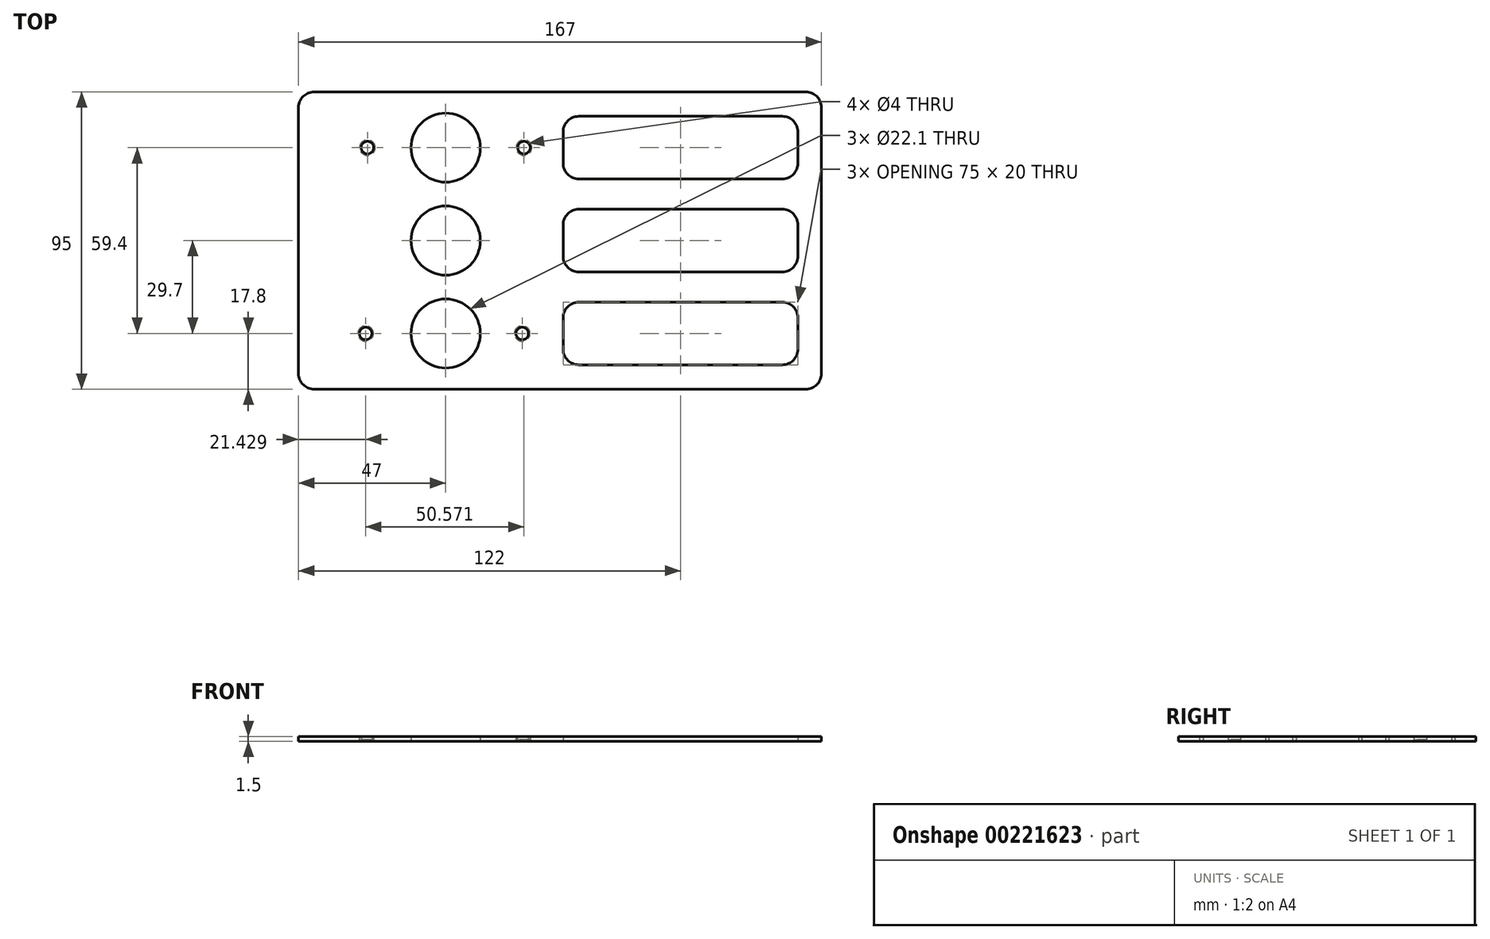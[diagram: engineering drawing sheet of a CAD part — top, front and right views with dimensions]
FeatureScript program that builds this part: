
annotation { "Feature Type Name" : "Feature", "Feature Type Description" : "" }
export const myFeature = defineFeature(function(context is Context, id is Id, definition is map)
    precondition{}
    {
        {
            var Q0;
            Q0=qCreatedBy(makeId("Top.planeOp"),FACE);
            var sketch = newSketch(context, id + "F0", { "sketchPlane" : qUnion([Q0])});
            skPoint(sketch, "E0.middle", {"position": v(0, 0) * mm});
            skCircle(sketch, "E1", {"center": v(-25, 29.7) * mm, "radius": 2 * mm});
            skCircle(sketch, "E2", {"center": v(25, 29.7) * mm, "radius": 2 * mm});
            skCircle(sketch, "E3", {"center": v(-25.57, -29.7) * mm, "radius": 2 * mm});
            skCircle(sketch, "E4", {"center": v(24.43, -29.7) * mm, "radius": 2 * mm});
            skLineSegment(sketch, "E5.bottom", {"start": v(-47, 47.5) * mm, "end": v(120, 47.5) * mm});
            skLineSegment(sketch, "E5.top", {"start": v(-47, -47.5) * mm, "end": v(120, -47.5) * mm});
            skLineSegment(sketch, "E5.left", {"start": v(-47, 47.5) * mm, "end": v(-47, -47.5) * mm});
            skLineSegment(sketch, "E5.right", {"start": v(120, 47.5) * mm, "end": v(120, -47.5) * mm});
            skPoint(sketch, "E5.middle", {"position": v(36.5, 0) * mm});
            skCircle(sketch, "E6", {"center": v(0, 29.7) * mm, "radius": 11.05 * mm});
            skCircle(sketch, "E7", {"center": v(0, 0) * mm, "radius": 11.05 * mm});
            skCircle(sketch, "E8", {"center": v(0, -29.7) * mm, "radius": 11.05 * mm});
            skLineSegment(sketch, "E9.bottom", {"start": v(112.5, 39.7) * mm, "end": v(37.5, 39.7) * mm});
            skLineSegment(sketch, "E9.top", {"start": v(112.5, 19.7) * mm, "end": v(37.5, 19.7) * mm});
            skLineSegment(sketch, "E9.left", {"start": v(112.5, 39.7) * mm, "end": v(112.5, 19.7) * mm});
            skLineSegment(sketch, "E9.right", {"start": v(37.5, 39.7) * mm, "end": v(37.5, 19.7) * mm});
            skPoint(sketch, "E9.middle", {"position": v(75, 29.7) * mm});
            skLineSegment(sketch, "E10.bottom", {"start": v(112.5, 10) * mm, "end": v(37.5, 10) * mm});
            skLineSegment(sketch, "E10.top", {"start": v(112.5, -10) * mm, "end": v(37.5, -10) * mm});
            skLineSegment(sketch, "E10.left", {"start": v(112.5, 10) * mm, "end": v(112.5, -10) * mm});
            skLineSegment(sketch, "E10.right", {"start": v(37.5, 10) * mm, "end": v(37.5, -10) * mm});
            skPoint(sketch, "E10.middle", {"position": v(75, 0) * mm});
            skPoint(sketch, "E10.middle.positionSnap0", {"position": v(75, 19.7) * mm});
            skPoint(sketch, "E10.centerSnap0", {"position": v(75, 19.7) * mm});
            skLineSegment(sketch, "E11.bottom", {"start": v(112.5, -19.7) * mm, "end": v(37.5, -19.7) * mm});
            skLineSegment(sketch, "E11.top", {"start": v(112.5, -39.7) * mm, "end": v(37.5, -39.7) * mm});
            skLineSegment(sketch, "E11.left", {"start": v(112.5, -19.7) * mm, "end": v(112.5, -39.7) * mm});
            skLineSegment(sketch, "E11.right", {"start": v(37.5, -19.7) * mm, "end": v(37.5, -39.7) * mm});
            skPoint(sketch, "E11.middle", {"position": v(75, -29.7) * mm});
            skSolve(sketch);
        }
        {
            var Q0;
            Q0=makeQuery(id+"F0.imprint","IMPRINT",FACE,{"disambiguationData":[TD([[makeQuery(id+"F0.imprint","IMPRINT",EDGE,{"derivedFrom":sQuery(id+"F0.wireOp",EDGE,"NzcNvOOA-lG1h-x87r-AjBX-t4IytyfyV268")}),-1.0]])]});
            var Q1;
            Q1=makeQuery(id+"F0.imprint","IMPRINT",FACE,{"disambiguationData":[TD([[makeQuery(id+"F0.imprint","IMPRINT",EDGE,{"derivedFrom":sQuery(id+"F0.wireOp",EDGE,"E1")}),-1.0]])]});
            extrude(context, id + "F1", {"entities" : qUnion([Q0, Q1]), "endBound" : BoundingType.SYMMETRIC, "offsetDistance" : 25 * mm, "depth" : 1.5 * mm});
        }
        {
            var Q0;
            Q0=makeQuery(id+"F1.opExtrude","SWEPT_EDGE",EDGE,{"disambiguationData":[OSD([sQuery(id+"F0.wireOp",EDGE,"E5.bottom"),sQuery(id+"F0.wireOp",EDGE,"E5.right")])]});
            var Q1;
            Q1=makeQuery(id+"F1.opExtrude","SWEPT_EDGE",EDGE,{"disambiguationData":[OSD([sQuery(id+"F0.wireOp",EDGE,"E5.top"),sQuery(id+"F0.wireOp",EDGE,"E5.right")])]});
            var Q2;
            Q2=makeQuery(id+"F1.opExtrude","SWEPT_EDGE",EDGE,{"disambiguationData":[OSD([sQuery(id+"F0.wireOp",EDGE,"E5.top"),sQuery(id+"F0.wireOp",EDGE,"E5.left")])]});
            var Q3;
            Q3=makeQuery(id+"F1.opExtrude","SWEPT_EDGE",EDGE,{"disambiguationData":[OSD([sQuery(id+"F0.wireOp",EDGE,"E5.bottom"),sQuery(id+"F0.wireOp",EDGE,"E5.left")])]});
            fillet(context, id + "F2", {"entities" : qUnion([Q0, Q1, Q2, Q3]), "radius" : 5 * mm, "tangentPropagation" : true, "allowEdgeOverflow" : false});
        }
        {
            var Q0;
            Q0=makeQuery(id+"F1.opExtrude","SWEPT_EDGE",EDGE,{"disambiguationData":[OSD([sQuery(id+"F0.wireOp",EDGE,"E9.bottom"),sQuery(id+"F0.wireOp",EDGE,"E9.right")])]});
            var Q1;
            Q1=makeQuery(id+"F1.opExtrude","SWEPT_EDGE",EDGE,{"disambiguationData":[OSD([sQuery(id+"F0.wireOp",EDGE,"E10.bottom"),sQuery(id+"F0.wireOp",EDGE,"E10.right")])]});
            var Q2;
            Q2=makeQuery(id+"F1.opExtrude","SWEPT_EDGE",EDGE,{"disambiguationData":[OSD([sQuery(id+"F0.wireOp",EDGE,"E11.bottom"),sQuery(id+"F0.wireOp",EDGE,"E11.right")])]});
            var Q3;
            Q3=makeQuery(id+"F1.opExtrude","SWEPT_EDGE",EDGE,{"disambiguationData":[OSD([sQuery(id+"F0.wireOp",EDGE,"E9.bottom"),sQuery(id+"F0.wireOp",EDGE,"E9.left")])]});
            var Q4;
            Q4=makeQuery(id+"F1.opExtrude","SWEPT_EDGE",EDGE,{"disambiguationData":[OSD([sQuery(id+"F0.wireOp",EDGE,"E10.bottom"),sQuery(id+"F0.wireOp",EDGE,"E10.left")])]});
            var Q5;
            Q5=makeQuery(id+"F1.opExtrude","SWEPT_EDGE",EDGE,{"disambiguationData":[OSD([sQuery(id+"F0.wireOp",EDGE,"E11.bottom"),sQuery(id+"F0.wireOp",EDGE,"E11.left")])]});
            var Q6;
            Q6=makeQuery(id+"F1.opExtrude","SWEPT_EDGE",EDGE,{"disambiguationData":[OSD([sQuery(id+"F0.wireOp",EDGE,"E11.top"),sQuery(id+"F0.wireOp",EDGE,"E11.left")])]});
            var Q7;
            Q7=makeQuery(id+"F1.opExtrude","SWEPT_EDGE",EDGE,{"disambiguationData":[OSD([sQuery(id+"F0.wireOp",EDGE,"E10.top"),sQuery(id+"F0.wireOp",EDGE,"E10.left")])]});
            var Q8;
            Q8=makeQuery(id+"F1.opExtrude","SWEPT_EDGE",EDGE,{"disambiguationData":[OSD([sQuery(id+"F0.wireOp",EDGE,"E9.top"),sQuery(id+"F0.wireOp",EDGE,"E9.left")])]});
            var Q9;
            Q9=makeQuery(id+"F1.opExtrude","SWEPT_EDGE",EDGE,{"disambiguationData":[OSD([sQuery(id+"F0.wireOp",EDGE,"E11.top"),sQuery(id+"F0.wireOp",EDGE,"E11.right")])]});
            var Q10;
            Q10=makeQuery(id+"F1.opExtrude","SWEPT_EDGE",EDGE,{"disambiguationData":[OSD([sQuery(id+"F0.wireOp",EDGE,"E10.top"),sQuery(id+"F0.wireOp",EDGE,"E10.right")])]});
            var Q11;
            Q11=makeQuery(id+"F1.opExtrude","SWEPT_EDGE",EDGE,{"disambiguationData":[OSD([sQuery(id+"F0.wireOp",EDGE,"E9.top"),sQuery(id+"F0.wireOp",EDGE,"E9.right")])]});
            fillet(context, id + "F3", {"entities" : qUnion([Q0, Q1, Q2, Q3, Q4, Q5, Q6, Q7, Q8, Q9, Q10, Q11]), "radius" : 5 * mm, "tangentPropagation" : true, "allowEdgeOverflow" : false});
        }
        {
            var Q0;
            Q0=makeQuery(id+"F1.opExtrude","CAP_EDGE",EDGE,{"disambiguationData":[OSD([sQuery(id+"F0.wireOp",EDGE,"E3")])],"isStart":true});
            var Q1;
            Q1=makeQuery(id+"F1.opExtrude","CAP_EDGE",EDGE,{"disambiguationData":[OSD([sQuery(id+"F0.wireOp",EDGE,"E4")])],"isStart":true});
            var Q2;
            Q2=makeQuery(id+"F1.opExtrude","CAP_EDGE",EDGE,{"disambiguationData":[OSD([sQuery(id+"F0.wireOp",EDGE,"E2")])],"isStart":true});
            var Q3;
            Q3=makeQuery(id+"F1.opExtrude","CAP_EDGE",EDGE,{"disambiguationData":[OSD([sQuery(id+"F0.wireOp",EDGE,"E1")])],"isStart":true});
            chamfer(context, id + "F4", {"entities" : qUnion([Q0, Q1, Q2, Q3]), "width" : 0.5 * mm, "tangentPropagation" : true});
        }
    });
